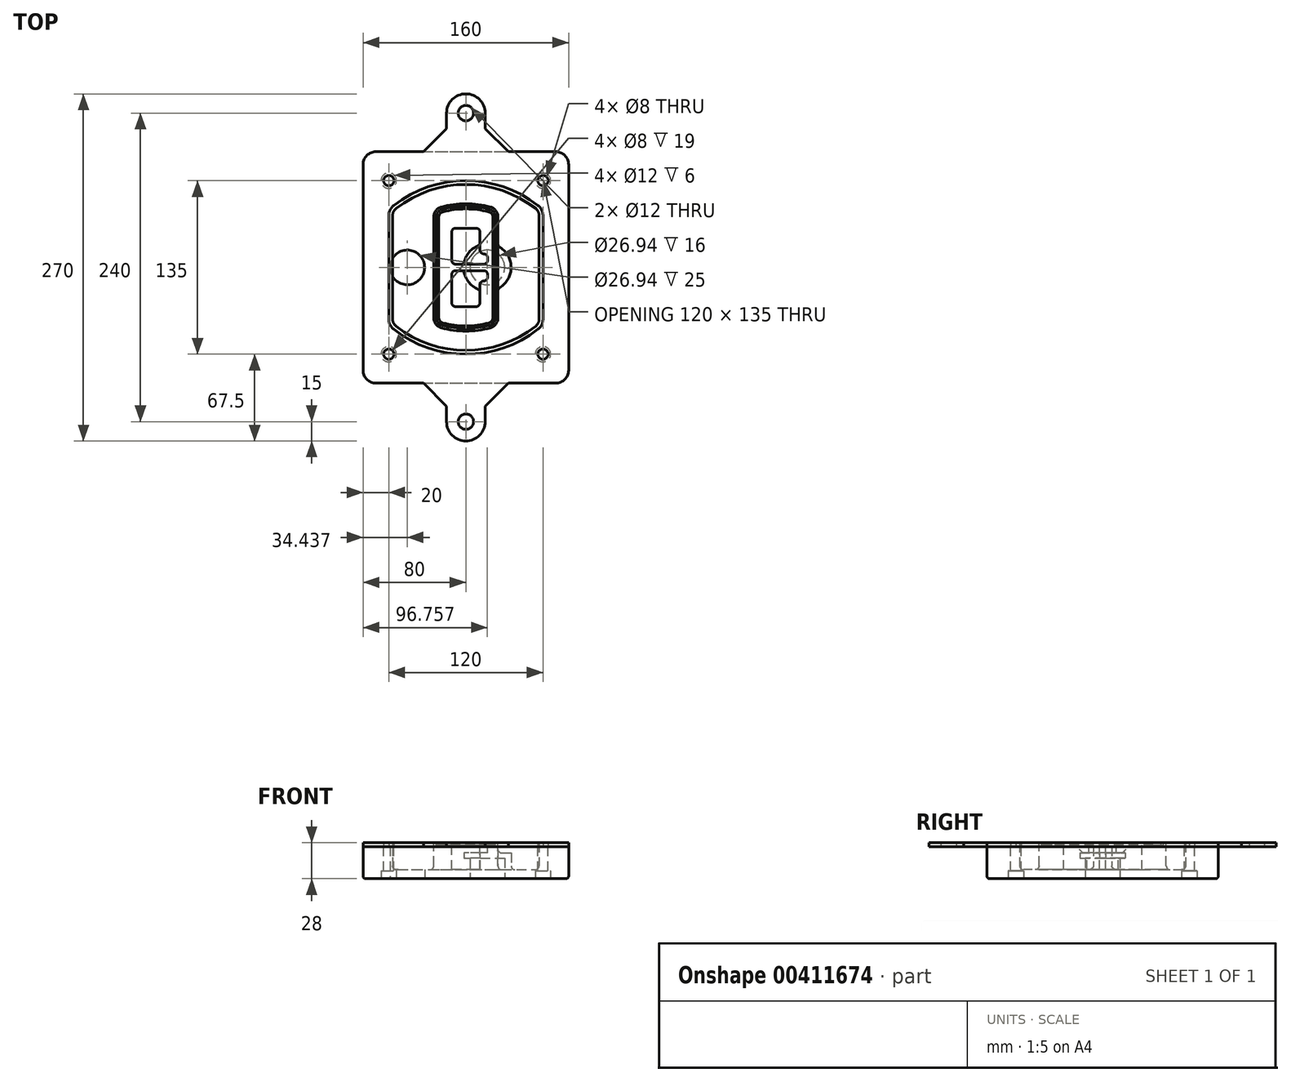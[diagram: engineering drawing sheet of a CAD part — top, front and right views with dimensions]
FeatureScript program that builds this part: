
annotation { "Feature Type Name" : "Feature", "Feature Type Description" : "" }
export const myFeature = defineFeature(function(context is Context, id is Id, definition is map)
    precondition{}
    {
        {
            var Q0;
            Q0=qCreatedBy(makeId("Top.planeOp"),FACE);
            var sketch = newSketch(context, id + "F0", { "sketchPlane" : qUnion([Q0])});
            skPoint(sketch, "E0.rect.middle", {"position": v(0, 0) * mm});
            skLineSegment(sketch, "E1.bottom", {"start": v(-70, -90) * mm, "end": v(70, -90) * mm});
            skLineSegment(sketch, "E1.top", {"start": v(-70, 90) * mm, "end": v(70, 90) * mm});
            skLineSegment(sketch, "E1.left", {"start": v(-80, -80) * mm, "end": v(-80, 80) * mm});
            skLineSegment(sketch, "E1.right", {"start": v(80, -80) * mm, "end": v(80, 80) * mm});
            skLineSegment(sketch, "E2", {"start": v(-80, 90) * mm, "end": v(80, -90) * mm, "construction": true});
            skLineSegment(sketch, "E3", {"start": v(80, 90) * mm, "end": v(-80, -90) * mm, "construction": true});
            skCircle(sketch, "E4", {"center": v(-60, 67.5) * mm, "radius": 4 * mm});
            skCircle(sketch, "E5", {"center": v(60, 67.5) * mm, "radius": 4 * mm});
            skCircle(sketch, "E6", {"center": v(60, -67.5) * mm, "radius": 4 * mm});
            skCircle(sketch, "E7", {"center": v(-60, -67.5) * mm, "radius": 4 * mm});
            skLineSegment(sketch, "E8", {"start": v(-60, 67.5) * mm, "end": v(60, 67.5) * mm, "construction": true});
            skLineSegment(sketch, "E9", {"start": v(60, 67.5) * mm, "end": v(60, -67.5) * mm, "construction": true});
            skLineSegment(sketch, "E10", {"start": v(60, -67.5) * mm, "end": v(-60, -67.5) * mm, "construction": true});
            skLineSegment(sketch, "E11", {"start": v(-60, -67.5) * mm, "end": v(-60, 67.5) * mm, "construction": true});
            skLineSegment(sketch, "E12", {"start": v(-60, 40.3) * mm, "end": v(-60, -40.3) * mm});
            skLineSegment(sketch, "E13", {"start": v(60, 40.3) * mm, "end": v(60, -40.3) * mm});
            skArc(sketch, "E14", {"start": v(56.15, 48.18) * mm, "mid": v(0, 67.5) * mm, "end": v(-56.15, 48.18) * mm});
            skArc(sketch, "E15", {"start": v(-56.15, -48.18) * mm, "mid": v(0, -67.5) * mm, "end": v(56.15, -48.18) * mm});
            skLineSegment(sketch, "E16", {"start": v(-60, 0) * mm, "end": v(60, 0) * mm, "construction": true});
            skPoint(sketch, "E17.visualSharp", {"position": v(-60, -45) * mm});
            skArc(sketch, "E17.filletArc", {"start": v(-60, -40.3) * mm, "mid": v(-58.99, -44.68) * mm, "end": v(-56.15, -48.18) * mm});
            skPoint(sketch, "E18.visualSharp", {"position": v(-60, 45) * mm});
            skArc(sketch, "E18.filletArc", {"start": v(-56.15, 48.18) * mm, "mid": v(-58.99, 44.68) * mm, "end": v(-60, 40.3) * mm});
            skPoint(sketch, "E19.visualSharp", {"position": v(60, 45) * mm});
            skArc(sketch, "E19.filletArc", {"start": v(60, 40.3) * mm, "mid": v(58.99, 44.68) * mm, "end": v(56.15, 48.18) * mm});
            skPoint(sketch, "E20.visualSharp", {"position": v(60, -45) * mm});
            skArc(sketch, "E20.filletArc", {"start": v(56.15, -48.18) * mm, "mid": v(58.99, -44.68) * mm, "end": v(60, -40.3) * mm});
            skPoint(sketch, "E21.visualSharp", {"position": v(-80, 90) * mm});
            skArc(sketch, "E21.filletArc", {"start": v(-70, 90) * mm, "mid": v(-77.07, 87.07) * mm, "end": v(-80, 80) * mm});
            skPoint(sketch, "E22.visualSharp", {"position": v(80, 90) * mm});
            skArc(sketch, "E22.filletArc", {"start": v(80, 80) * mm, "mid": v(77.07, 87.07) * mm, "end": v(70, 90) * mm});
            skPoint(sketch, "E23.visualSharp", {"position": v(80, -90) * mm});
            skArc(sketch, "E23.filletArc", {"start": v(70, -90) * mm, "mid": v(77.07, -87.07) * mm, "end": v(80, -80) * mm});
            skPoint(sketch, "E24.visualSharp", {"position": v(-80, -90) * mm});
            skArc(sketch, "E24.filletArc", {"start": v(-80, -80) * mm, "mid": v(-77.07, -87.07) * mm, "end": v(-70, -90) * mm});
            skArc(sketch, "E25.0", {"start": v(57, 40.3) * mm, "mid": v(56.3, 43.36) * mm, "end": v(54.3, 45.81) * mm});
            skLineSegment(sketch, "E25.1", {"start": v(57, 40.3) * mm, "end": v(57, -40.3) * mm});
            skArc(sketch, "E25.2", {"start": v(54.3, -45.81) * mm, "mid": v(56.3, -43.36) * mm, "end": v(57, -40.3) * mm});
            skArc(sketch, "E25.3", {"start": v(-54.3, -45.81) * mm, "mid": v(0, -64.5) * mm, "end": v(54.3, -45.81) * mm});
            skArc(sketch, "E25.4", {"start": v(-57, -40.3) * mm, "mid": v(-56.3, -43.36) * mm, "end": v(-54.3, -45.81) * mm});
            skArc(sketch, "E25.5", {"start": v(54.3, 45.81) * mm, "mid": v(0, 64.5) * mm, "end": v(-54.3, 45.81) * mm});
            skLineSegment(sketch, "E25.6", {"start": v(-57, 40.3) * mm, "end": v(-57, -40.3) * mm});
            skArc(sketch, "E25.7", {"start": v(-54.3, 45.81) * mm, "mid": v(-56.3, 43.36) * mm, "end": v(-57, 40.3) * mm});
            skArc(sketch, "E26.0", {"start": v(-58.62, 51.33) * mm, "mid": v(-62.58, 46.43) * mm, "end": v(-64, 40.3) * mm});
            skArc(sketch, "E26.1", {"start": v(58.62, 51.33) * mm, "mid": v(0, 71.5) * mm, "end": v(-58.62, 51.33) * mm});
            skArc(sketch, "E26.2", {"start": v(64, 40.3) * mm, "mid": v(62.58, 46.43) * mm, "end": v(58.62, 51.33) * mm});
            skLineSegment(sketch, "E26.3", {"start": v(64, 40.3) * mm, "end": v(64, -40.3) * mm});
            skArc(sketch, "E26.4", {"start": v(58.62, -51.33) * mm, "mid": v(62.58, -46.43) * mm, "end": v(64, -40.3) * mm});
            skLineSegment(sketch, "E26.5", {"start": v(-64, 40.3) * mm, "end": v(-64, -40.3) * mm});
            skArc(sketch, "E26.6", {"start": v(-58.62, -51.33) * mm, "mid": v(0, -71.5) * mm, "end": v(58.62, -51.33) * mm});
            skArc(sketch, "E26.7", {"start": v(-64, -40.3) * mm, "mid": v(-62.58, -46.43) * mm, "end": v(-58.62, -51.33) * mm});
            skSolve(sketch);
        }
        {
            var Q0;
            Q0=makeQuery(id+"F0.imprint","IMPRINT",FACE,{"disambiguationData":[TD([[makeQuery(id+"F0.imprint","IMPRINT",EDGE,{"derivedFrom":sQuery(id+"F0.wireOp",EDGE,"E1.bottom")}),1.0]])]});
            var Q1;
            Q1=makeQuery(id+"F0.imprint","IMPRINT",FACE,{"disambiguationData":[TD([[makeQuery(id+"F0.imprint","IMPRINT",EDGE,{"derivedFrom":sQuery(id+"F0.wireOp",EDGE,"E12")}),1.0]])]});
            var Q2;
            Q2=makeQuery(id+"F0.imprint","IMPRINT",FACE,{"disambiguationData":[TD([[makeQuery(id+"F0.imprint","IMPRINT",EDGE,{"derivedFrom":sQuery(id+"F0.wireOp",EDGE,"E25.0")}),1.0]])]});
            var Q3;
            Q3=makeQuery(id+"F0.imprint","IMPRINT",FACE,{"disambiguationData":[TD([[makeQuery(id+"F0.imprint","IMPRINT",EDGE,{"derivedFrom":sQuery(id+"F0.wireOp",EDGE,"E12")}),-1.0]])]});
            extrude(context, id + "F1", {"entities" : qUnion([Q0, Q1, Q2, Q3]), "oppositeDirection" : true, "depth" : 25 * mm});
        }
        {
            var Q0;
            Q0=makeQuery(id+"F0.imprint","IMPRINT",FACE,{"disambiguationData":[TD([[makeQuery(id+"F0.imprint","IMPRINT",EDGE,{"derivedFrom":sQuery(id+"F0.wireOp",EDGE,"E12")}),1.0]])]});
            extrude(context, id + "F2", {"entities" : qUnion([Q0]), "operationType" : NewBodyOperationType.ADD, "depth" : 3 * mm});
        }
        {
            var Q0;
            Q0=makeQuery(id+"F0.imprint","IMPRINT",FACE,{"disambiguationData":[TD([[makeQuery(id+"F0.imprint","IMPRINT",EDGE,{"derivedFrom":sQuery(id+"F0.wireOp",EDGE,"E25.0")}),1.0]])]});
            extrude(context, id + "F3", {"entities" : qUnion([Q0]), "operationType" : NewBodyOperationType.REMOVE, "oppositeDirection" : true, "depth" : 18 * mm});
        }
        {
            var Q0;
            Q0=makeQuery(id+"F2.opExtrude","CAP_FACE",FACE,{"disambiguationData":[OSD([sQuery(id+"F0.wireOp",EDGE,"E12"),sQuery(id+"F0.wireOp",EDGE,"E13"),sQuery(id+"F0.wireOp",EDGE,"E14"),sQuery(id+"F0.wireOp",EDGE,"E15"),sQuery(id+"F0.wireOp",EDGE,"E17.filletArc"),sQuery(id+"F0.wireOp",EDGE,"E18.filletArc"),sQuery(id+"F0.wireOp",EDGE,"E19.filletArc"),sQuery(id+"F0.wireOp",EDGE,"E20.filletArc"),sQuery(id+"F0.wireOp",EDGE,"E25.0"),sQuery(id+"F0.wireOp",EDGE,"E25.1"),sQuery(id+"F0.wireOp",EDGE,"E25.2"),sQuery(id+"F0.wireOp",EDGE,"E25.3"),sQuery(id+"F0.wireOp",EDGE,"E25.4"),sQuery(id+"F0.wireOp",EDGE,"E25.5"),sQuery(id+"F0.wireOp",EDGE,"E25.6"),sQuery(id+"F0.wireOp",EDGE,"E25.7")])],"isStart":false});
            var sketch = newSketch(context, id + "F4", { "sketchPlane" : qUnion([Q0])});
            skArc(sketch, "E27.0", {"start": v(-19.08, -46.97) * mm, "mid": v(0, -49.5) * mm, "end": v(19.08, -46.97) * mm});
            skArc(sketch, "E28.0", {"start": v(19.08, 46.97) * mm, "mid": v(0, 49.5) * mm, "end": v(-19.08, 46.97) * mm});
            skLineSegment(sketch, "E29", {"start": v(-25, 39.25) * mm, "end": v(-25, -39.25) * mm});
            skLineSegment(sketch, "E30", {"start": v(25, 39.25) * mm, "end": v(25, -39.25) * mm});
            skLineSegment(sketch, "E31", {"start": v(-25, 45.1) * mm, "end": v(25, 45.1) * mm, "construction": true});
            skLineSegment(sketch, "E32", {"start": v(-25, -45.1) * mm, "end": v(25, -45.1) * mm, "construction": true});
            skPoint(sketch, "E33.visualSharp", {"position": v(-25, 45.1) * mm});
            skArc(sketch, "E33.filletArc", {"start": v(-19.08, 46.97) * mm, "mid": v(-23.35, 44.11) * mm, "end": v(-25, 39.25) * mm});
            skPoint(sketch, "E34.visualSharp", {"position": v(25, 45.1) * mm});
            skArc(sketch, "E34.filletArc", {"start": v(25, 39.25) * mm, "mid": v(23.35, 44.11) * mm, "end": v(19.08, 46.97) * mm});
            skPoint(sketch, "E35.visualSharp", {"position": v(25, -45.1) * mm});
            skArc(sketch, "E35.filletArc", {"start": v(19.08, -46.97) * mm, "mid": v(23.35, -44.11) * mm, "end": v(25, -39.25) * mm});
            skPoint(sketch, "E36.visualSharp", {"position": v(-25, -45.1) * mm});
            skArc(sketch, "E36.filletArc", {"start": v(-25, -39.25) * mm, "mid": v(-23.35, -44.11) * mm, "end": v(-19.08, -46.97) * mm});
            skArc(sketch, "E37.0", {"start": v(54.3, 45.81) * mm, "mid": v(0, 64.5) * mm, "end": v(-54.3, 45.81) * mm});
            skArc(sketch, "E37.1", {"start": v(-54.3, 45.81) * mm, "mid": v(-56.3, 43.36) * mm, "end": v(-57, 40.3) * mm});
            skLineSegment(sketch, "E37.2", {"start": v(-57, 40.3) * mm, "end": v(-57, -40.3) * mm});
            skArc(sketch, "E37.3", {"start": v(-57, -40.3) * mm, "mid": v(-56.3, -43.36) * mm, "end": v(-54.3, -45.81) * mm});
            skArc(sketch, "E37.4", {"start": v(-54.3, -45.81) * mm, "mid": v(0, -64.5) * mm, "end": v(54.3, -45.81) * mm});
            skArc(sketch, "E37.5", {"start": v(54.3, -45.81) * mm, "mid": v(56.3, -43.36) * mm, "end": v(57, -40.3) * mm});
            skLineSegment(sketch, "E37.6", {"start": v(57, 40.3) * mm, "end": v(57, -40.3) * mm});
            skArc(sketch, "E37.7", {"start": v(57, 40.3) * mm, "mid": v(56.3, 43.36) * mm, "end": v(54.3, 45.81) * mm});
            skLineSegment(sketch, "E38.0", {"start": v(23, 39.25) * mm, "end": v(23, -39.25) * mm});
            skArc(sketch, "E38.1", {"start": v(18.56, -45.04) * mm, "mid": v(21.76, -42.9) * mm, "end": v(23, -39.25) * mm});
            skArc(sketch, "E38.2", {"start": v(-18.56, -45.04) * mm, "mid": v(0, -47.5) * mm, "end": v(18.56, -45.04) * mm});
            skArc(sketch, "E38.3", {"start": v(-23, -39.25) * mm, "mid": v(-21.76, -42.9) * mm, "end": v(-18.56, -45.04) * mm});
            skLineSegment(sketch, "E38.4", {"start": v(-23, 39.25) * mm, "end": v(-23, -39.25) * mm});
            skArc(sketch, "E38.5", {"start": v(23, 39.25) * mm, "mid": v(21.76, 42.9) * mm, "end": v(18.56, 45.04) * mm});
            skArc(sketch, "E38.6", {"start": v(-18.56, 45.04) * mm, "mid": v(-21.76, 42.9) * mm, "end": v(-23, 39.25) * mm});
            skArc(sketch, "E38.7", {"start": v(18.56, 45.04) * mm, "mid": v(0, 47.5) * mm, "end": v(-18.56, 45.04) * mm});
            skArc(sketch, "E39.0", {"start": v(21, 39.25) * mm, "mid": v(20.18, 41.68) * mm, "end": v(18.04, 43.1) * mm});
            skLineSegment(sketch, "E39.1", {"start": v(21, 39.25) * mm, "end": v(21, -39.25) * mm});
            skArc(sketch, "E39.2", {"start": v(18.04, -43.1) * mm, "mid": v(20.18, -41.68) * mm, "end": v(21, -39.25) * mm});
            skArc(sketch, "E39.3", {"start": v(-18.04, -43.1) * mm, "mid": v(0, -45.5) * mm, "end": v(18.04, -43.1) * mm});
            skArc(sketch, "E39.4", {"start": v(-21, -39.25) * mm, "mid": v(-20.18, -41.68) * mm, "end": v(-18.04, -43.1) * mm});
            skArc(sketch, "E39.5", {"start": v(18.04, 43.1) * mm, "mid": v(0, 45.5) * mm, "end": v(-18.04, 43.1) * mm});
            skLineSegment(sketch, "E39.6", {"start": v(-21, 39.25) * mm, "end": v(-21, -39.25) * mm});
            skArc(sketch, "E39.7", {"start": v(-18.04, 43.1) * mm, "mid": v(-20.18, 41.68) * mm, "end": v(-21, 39.25) * mm});
            skLineSegment(sketch, "E40", {"start": v(-25, 0) * mm, "end": v(25, 0) * mm, "construction": true});
            skLineSegment(sketch, "E41", {"start": v(-11, 5.5) * mm, "end": v(-11, 27.5) * mm});
            skLineSegment(sketch, "E42", {"start": v(-8, 30.5) * mm, "end": v(8, 30.5) * mm});
            skLineSegment(sketch, "E43", {"start": v(11, 27.5) * mm, "end": v(11, 13.5) * mm});
            skLineSegment(sketch, "E44", {"start": v(14, 10.5) * mm, "end": v(14, 10.5) * mm});
            skLineSegment(sketch, "E45", {"start": v(17, 7.5) * mm, "end": v(17, 5.5) * mm});
            skLineSegment(sketch, "E46", {"start": v(14, 2.5) * mm, "end": v(-8, 2.5) * mm});
            skPoint(sketch, "E47.visualSharp", {"position": v(-11, 30.5) * mm});
            skArc(sketch, "E47.filletArc", {"start": v(-8, 30.5) * mm, "mid": v(-10.12, 29.62) * mm, "end": v(-11, 27.5) * mm});
            skPoint(sketch, "E48.visualSharp", {"position": v(11, 30.5) * mm});
            skArc(sketch, "E48.filletArc", {"start": v(11, 27.5) * mm, "mid": v(10.12, 29.62) * mm, "end": v(8, 30.5) * mm});
            skPoint(sketch, "E49.visualSharp", {"position": v(11, 10.5) * mm});
            skArc(sketch, "E49.filletArc", {"start": v(11, 13.5) * mm, "mid": v(11.88, 11.38) * mm, "end": v(14, 10.5) * mm});
            skPoint(sketch, "E50.visualSharp", {"position": v(17, 10.5) * mm});
            skArc(sketch, "E50.filletArc", {"start": v(17, 7.5) * mm, "mid": v(16.12, 9.62) * mm, "end": v(14, 10.5) * mm});
            skPoint(sketch, "E51.visualSharp", {"position": v(17, 2.5) * mm});
            skArc(sketch, "E51.filletArc", {"start": v(14, 2.5) * mm, "mid": v(16.12, 3.38) * mm, "end": v(17, 5.5) * mm});
            skPoint(sketch, "E52.visualSharp", {"position": v(-11, 2.5) * mm});
            skArc(sketch, "E52.filletArc", {"start": v(-11, 5.5) * mm, "mid": v(-10.12, 3.38) * mm, "end": v(-8, 2.5) * mm});
            skLineSegment(sketch, "E53.0.MirrorCS", {"start": v(14, -2.5) * mm, "end": v(-8, -2.5) * mm});
            skArc(sketch, "E54.0.MirrorCS", {"start": v(-11, -5.5) * mm, "mid": v(-10.12, -3.38) * mm, "end": v(-8, -2.5) * mm});
            skLineSegment(sketch, "E55.0.MirrorCS", {"start": v(-11, -5.5) * mm, "end": v(-11, -27.5) * mm});
            skArc(sketch, "E56.0.MirrorCS", {"start": v(-8, -30.5) * mm, "mid": v(-10.12, -29.62) * mm, "end": v(-11, -27.5) * mm});
            skLineSegment(sketch, "E57.0.MirrorCS", {"start": v(-8, -30.5) * mm, "end": v(8, -30.5) * mm});
            skArc(sketch, "E58.0.MirrorCS", {"start": v(11, -27.5) * mm, "mid": v(10.12, -29.62) * mm, "end": v(8, -30.5) * mm});
            skLineSegment(sketch, "E59.0.MirrorCS", {"start": v(11, -27.5) * mm, "end": v(11, -13.5) * mm});
            skArc(sketch, "E60.0.MirrorCS", {"start": v(11, -13.5) * mm, "mid": v(11.88, -11.38) * mm, "end": v(14, -10.5) * mm});
            skArc(sketch, "E61.0.MirrorCS", {"start": v(17, -7.5) * mm, "mid": v(16.12, -9.62) * mm, "end": v(14, -10.5) * mm});
            skLineSegment(sketch, "E62.0.MirrorCS", {"start": v(17, -7.5) * mm, "end": v(17, -5.5) * mm});
            skArc(sketch, "E63.0.MirrorCS", {"start": v(14, -2.5) * mm, "mid": v(16.12, -3.38) * mm, "end": v(17, -5.5) * mm});
            skSolve(sketch);
        }
        {
            var Q0;
            Q0=makeQuery(id+"F4.imprint","IMPRINT",FACE,{"disambiguationData":[TD([[makeQuery(id+"F4.imprint","IMPRINT",EDGE,{"derivedFrom":sQuery(id+"F4.wireOp",EDGE,"E27.0")}),1.0]])]});
            var Q1;
            Q1=makeQuery(id+"F4.imprint","IMPRINT",FACE,{"disambiguationData":[TD([[makeQuery(id+"F4.imprint","IMPRINT",EDGE,{"derivedFrom":sQuery(id+"F4.wireOp",EDGE,"E38.0")}),-1.0]])]});
            var Q2;
            Q2=makeQuery(id+"F4.imprint","IMPRINT",FACE,{"disambiguationData":[TD([[makeQuery(id+"F4.imprint","IMPRINT",EDGE,{"derivedFrom":sQuery(id+"F4.wireOp",EDGE,"E39.0")}),1.0]])]});
            extrude(context, id + "F5", {"entities" : qUnion([Q0, Q1, Q2]), "operationType" : NewBodyOperationType.ADD, "endBound" : BoundingType.UP_TO_NEXT, "oppositeDirection" : true, "depth" : 25 * mm});
        }
        {
            var Q0;
            Q0=makeQuery(id+"F4.imprint","IMPRINT",FACE,{"disambiguationData":[TD([[makeQuery(id+"F4.imprint","IMPRINT",EDGE,{"derivedFrom":sQuery(id+"F4.wireOp",EDGE,"E38.0")}),-1.0]])]});
            extrude(context, id + "F6", {"entities" : qUnion([Q0]), "operationType" : NewBodyOperationType.REMOVE, "oppositeDirection" : true, "depth" : 2 * mm});
        }
        {
            var Q0;
            Q0=makeQuery(id+"F1.opExtrude","CAP_FACE",FACE,{"disambiguationData":[OSD([sQuery(id+"F0.wireOp",EDGE,"E1.bottom"),sQuery(id+"F0.wireOp",EDGE,"E1.top"),sQuery(id+"F0.wireOp",EDGE,"E1.left"),sQuery(id+"F0.wireOp",EDGE,"E1.right"),sQuery(id+"F0.wireOp",EDGE,"E4"),sQuery(id+"F0.wireOp",EDGE,"E5"),sQuery(id+"F0.wireOp",EDGE,"E6"),sQuery(id+"F0.wireOp",EDGE,"E7"),sQuery(id+"F0.wireOp",EDGE,"E21.filletArc"),sQuery(id+"F0.wireOp",EDGE,"E22.filletArc"),sQuery(id+"F0.wireOp",EDGE,"E23.filletArc"),sQuery(id+"F0.wireOp",EDGE,"E24.filletArc")])],"isStart":false});
            var sketch = newSketch(context, id + "F7", { "sketchPlane" : qUnion([Q0])});
            skCircle(sketch, "E64", {"center": v(16.76, 0) * mm, "radius": 13.47 * mm});
            skCircle(sketch, "E65", {"center": v(-45.56, 0) * mm, "radius": 13.47 * mm});
            skLineSegment(sketch, "E66", {"start": v(80, 0) * mm, "end": v(-80, 0) * mm});
            skCircle(sketch, "E67", {"center": v(16.76, 0) * mm, "radius": 18.47 * mm});
            skCircle(sketch, "E68", {"center": v(60, -67.5) * mm, "radius": 6 * mm});
            skCircle(sketch, "E69", {"center": v(-60, -67.5) * mm, "radius": 6 * mm});
            skCircle(sketch, "E70", {"center": v(-60, 67.5) * mm, "radius": 6 * mm});
            skCircle(sketch, "E71", {"center": v(60, 67.5) * mm, "radius": 6 * mm});
            skSolve(sketch);
        }
        {
            var Q0;
            {var subQ1=sQuery(id+"F7.wireOp",EDGE,"E66");var subQ4=sQuery(id+"F7.wireOp",EDGE,"E64");var subQ6=makeQuery(id+"F7.imprint","INTERSECT",VERTEX,{"disambiguationData":[OD(0.0)],"derivedFrom":[subQ4,subQ1]});Q0=makeQuery(id+"F7.imprint","IMPRINT",FACE,{"disambiguationData":[TD([[makeQuery(id+"F7.imprint","IMPRINT",EDGE,{"disambiguationData":[TD([[subQ6,-1.0]])],"derivedFrom":subQ4}),-1.0]])]});}
            var Q1;
            {var subQ0=sQuery(id+"F7.wireOp",EDGE,"E66");var subQ1=sQuery(id+"F7.wireOp",EDGE,"E64");var subQ3=makeQuery(id+"F7.imprint","INTERSECT",VERTEX,{"disambiguationData":[OD(0.0)],"derivedFrom":[subQ1,subQ0]});Q1=makeQuery(id+"F7.imprint","IMPRINT",FACE,{"disambiguationData":[TD([[makeQuery(id+"F7.imprint","IMPRINT",EDGE,{"disambiguationData":[TD([[subQ3,-1.0]])],"derivedFrom":subQ1}),1.0]])]});}
            var Q2;
            {var subQ0=sQuery(id+"F7.wireOp",EDGE,"E66");var subQ1=sQuery(id+"F7.wireOp",EDGE,"E64");var subQ3=makeQuery(id+"F7.imprint","INTERSECT",VERTEX,{"disambiguationData":[OD(0.0)],"derivedFrom":[subQ1,subQ0]});Q2=makeQuery(id+"F7.imprint","IMPRINT",FACE,{"disambiguationData":[TD([[makeQuery(id+"F7.imprint","IMPRINT",EDGE,{"disambiguationData":[TD([[subQ3,1.0]])],"derivedFrom":subQ1}),1.0]])]});}
            var Q3;
            {var subQ1=sQuery(id+"F7.wireOp",EDGE,"E66");var subQ4=sQuery(id+"F7.wireOp",EDGE,"E64");var subQ6=makeQuery(id+"F7.imprint","INTERSECT",VERTEX,{"disambiguationData":[OD(0.0)],"derivedFrom":[subQ4,subQ1]});Q3=makeQuery(id+"F7.imprint","IMPRINT",FACE,{"disambiguationData":[TD([[makeQuery(id+"F7.imprint","IMPRINT",EDGE,{"disambiguationData":[TD([[subQ6,1.0]])],"derivedFrom":subQ4}),-1.0]])]});}
            extrude(context, id + "F8", {"entities" : qUnion([Q0, Q1, Q2, Q3]), "operationType" : NewBodyOperationType.ADD, "oppositeDirection" : true, "depth" : 20 * mm});
        }
        {
            var Q0;
            {var subQ0=sQuery(id+"F7.wireOp",EDGE,"E66");var subQ1=sQuery(id+"F7.wireOp",EDGE,"E64");var subQ3=makeQuery(id+"F7.imprint","INTERSECT",VERTEX,{"disambiguationData":[OD(0.0)],"derivedFrom":[subQ1,subQ0]});Q0=makeQuery(id+"F7.imprint","IMPRINT",FACE,{"disambiguationData":[TD([[makeQuery(id+"F7.imprint","IMPRINT",EDGE,{"disambiguationData":[TD([[subQ3,-1.0]])],"derivedFrom":subQ1}),1.0]])]});}
            var Q1;
            {var subQ0=sQuery(id+"F7.wireOp",EDGE,"E66");var subQ1=sQuery(id+"F7.wireOp",EDGE,"E64");var subQ3=makeQuery(id+"F7.imprint","INTERSECT",VERTEX,{"disambiguationData":[OD(0.0)],"derivedFrom":[subQ1,subQ0]});Q1=makeQuery(id+"F7.imprint","IMPRINT",FACE,{"disambiguationData":[TD([[makeQuery(id+"F7.imprint","IMPRINT",EDGE,{"disambiguationData":[TD([[subQ3,1.0]])],"derivedFrom":subQ1}),1.0]])]});}
            extrude(context, id + "F9", {"entities" : qUnion([Q0, Q1]), "operationType" : NewBodyOperationType.REMOVE, "oppositeDirection" : true, "depth" : 16 * mm});
        }
        {
            var Q0;
            {var subQ0=sQuery(id+"F7.wireOp",EDGE,"E66");var subQ1=sQuery(id+"F7.wireOp",EDGE,"E65");var subQ3=makeQuery(id+"F7.imprint","INTERSECT",VERTEX,{"disambiguationData":[OD(0.0)],"derivedFrom":[subQ1,subQ0]});Q0=makeQuery(id+"F7.imprint","IMPRINT",FACE,{"disambiguationData":[TD([[makeQuery(id+"F7.imprint","IMPRINT",EDGE,{"disambiguationData":[TD([[subQ3,-1.0]])],"derivedFrom":subQ1}),1.0]])]});}
            var Q1;
            {var subQ0=sQuery(id+"F7.wireOp",EDGE,"E66");var subQ1=sQuery(id+"F7.wireOp",EDGE,"E65");var subQ3=makeQuery(id+"F7.imprint","INTERSECT",VERTEX,{"disambiguationData":[OD(0.0)],"derivedFrom":[subQ1,subQ0]});Q1=makeQuery(id+"F7.imprint","IMPRINT",FACE,{"disambiguationData":[TD([[makeQuery(id+"F7.imprint","IMPRINT",EDGE,{"disambiguationData":[TD([[subQ3,1.0]])],"derivedFrom":subQ1}),1.0]])]});}
            extrude(context, id + "F10", {"entities" : qUnion([Q0, Q1]), "operationType" : NewBodyOperationType.REMOVE, "oppositeDirection" : true, "depth" : 25 * mm});
        }
        {
            var Q0;
            Q0=makeQuery(id+"F7.imprint","IMPRINT",FACE,{"disambiguationData":[TD([[makeQuery(id+"F7.imprint","IMPRINT",EDGE,{"derivedFrom":sQuery(id+"F7.wireOp",EDGE,"E68")}),1.0]])]});
            var Q1;
            Q1=makeQuery(id+"F7.imprint","IMPRINT",FACE,{"disambiguationData":[TD([[makeQuery(id+"F7.imprint","IMPRINT",EDGE,{"derivedFrom":makeQuery(id+"F1.opExtrude","CAP_EDGE",EDGE,{"disambiguationData":[OSD([sQuery(id+"F0.wireOp",EDGE,"E5")])],"isStart":false})}),-1.0]])]});
            var Q2;
            Q2=makeQuery(id+"F7.imprint","IMPRINT",FACE,{"disambiguationData":[TD([[makeQuery(id+"F7.imprint","IMPRINT",EDGE,{"derivedFrom":sQuery(id+"F7.wireOp",EDGE,"E69")}),1.0]])]});
            var Q3;
            Q3=makeQuery(id+"F7.imprint","IMPRINT",FACE,{"disambiguationData":[TD([[makeQuery(id+"F7.imprint","IMPRINT",EDGE,{"derivedFrom":makeQuery(id+"F1.opExtrude","CAP_EDGE",EDGE,{"disambiguationData":[OSD([sQuery(id+"F0.wireOp",EDGE,"E4")])],"isStart":false})}),-1.0]])]});
            var Q4;
            Q4=makeQuery(id+"F7.imprint","IMPRINT",FACE,{"disambiguationData":[TD([[makeQuery(id+"F7.imprint","IMPRINT",EDGE,{"derivedFrom":sQuery(id+"F7.wireOp",EDGE,"E70")}),1.0]])]});
            var Q5;
            Q5=makeQuery(id+"F7.imprint","IMPRINT",FACE,{"disambiguationData":[TD([[makeQuery(id+"F7.imprint","IMPRINT",EDGE,{"derivedFrom":makeQuery(id+"F1.opExtrude","CAP_EDGE",EDGE,{"disambiguationData":[OSD([sQuery(id+"F0.wireOp",EDGE,"E7")])],"isStart":false})}),-1.0]])]});
            var Q6;
            Q6=makeQuery(id+"F7.imprint","IMPRINT",FACE,{"disambiguationData":[TD([[makeQuery(id+"F7.imprint","IMPRINT",EDGE,{"derivedFrom":sQuery(id+"F7.wireOp",EDGE,"E71")}),1.0]])]});
            var Q7;
            Q7=makeQuery(id+"F7.imprint","IMPRINT",FACE,{"disambiguationData":[TD([[makeQuery(id+"F7.imprint","IMPRINT",EDGE,{"derivedFrom":makeQuery(id+"F1.opExtrude","CAP_EDGE",EDGE,{"disambiguationData":[OSD([sQuery(id+"F0.wireOp",EDGE,"E6")])],"isStart":false})}),-1.0]])]});
            extrude(context, id + "F11", {"entities" : qUnion([Q0, Q1, Q2, Q3, Q4, Q5, Q6, Q7]), "operationType" : NewBodyOperationType.REMOVE, "oppositeDirection" : true, "depth" : 6 * mm});
        }
        {
            var Q0;
            Q0=makeQuery(id+"F9.boolean.opBoolean","COPY",FACE,{"derivedFrom":makeQuery(id+"F9.opExtrude","CAP_FACE",FACE,{"disambiguationData":[OSD([sQuery(id+"F7.wireOp",EDGE,"E64")])],"isStart":false})});
            var sketch = newSketch(context, id + "F12", { "sketchPlane" : qUnion([Q0])});
            skArc(sketch, "E72.0", {"start": v(11, 17.55) * mm, "mid": v(2.57, 11.82) * mm, "end": v(-1.54, 2.5) * mm});
            skArc(sketch, "E72.1", {"start": v(-1.54, -2.5) * mm, "mid": v(2.57, -11.82) * mm, "end": v(11, -17.55) * mm});
            skLineSegment(sketch, "E73", {"start": v(-1.54, -2.5) * mm, "end": v(14, -2.5) * mm});
            skLineSegment(sketch, "E74.0", {"start": v(14, 2.5) * mm, "end": v(-1.54, 2.5) * mm});
            skArc(sketch, "E74.1", {"start": v(14, 2.5) * mm, "mid": v(16.12, 3.38) * mm, "end": v(17, 5.5) * mm});
            skLineSegment(sketch, "E74.2", {"start": v(17, 7.5) * mm, "end": v(17, 5.5) * mm});
            skArc(sketch, "E74.3", {"start": v(17, 7.5) * mm, "mid": v(16.12, 9.62) * mm, "end": v(14, 10.5) * mm});
            skArc(sketch, "E74.4", {"start": v(11, 13.5) * mm, "mid": v(11.88, 11.38) * mm, "end": v(14, 10.5) * mm});
            skLineSegment(sketch, "E74.5", {"start": v(11, 17.55) * mm, "end": v(11, 13.5) * mm});
            skLineSegment(sketch, "E74.7", {"start": v(14, -2.5) * mm, "end": v(-1.54, -2.5) * mm});
            skArc(sketch, "E74.8", {"start": v(14, -2.5) * mm, "mid": v(16.12, -3.38) * mm, "end": v(17, -5.5) * mm});
            skLineSegment(sketch, "E74.9", {"start": v(17, -7.5) * mm, "end": v(17, -5.5) * mm});
            skArc(sketch, "E74.10", {"start": v(17, -7.5) * mm, "mid": v(16.12, -9.62) * mm, "end": v(14, -10.5) * mm});
            skArc(sketch, "E74.11", {"start": v(11, -13.5) * mm, "mid": v(11.88, -11.38) * mm, "end": v(14, -10.5) * mm});
            skLineSegment(sketch, "E74.12", {"start": v(11, -17.55) * mm, "end": v(11, -13.5) * mm});
            skPoint(sketch, "E75.orphan", {"position": v(11, -27.5) * mm});
            skPoint(sketch, "E76.orphan", {"position": v(-8, -2.5) * mm});
            skPoint(sketch, "E77.orphan", {"position": v(-8, 2.5) * mm});
            skPoint(sketch, "E78.orphan", {"position": v(11, 27.5) * mm});
            skSolve(sketch);
        }
        {
            var Q0;
            {var subQ7=sQuery(id+"F12.wireOp",EDGE,"E72.0");var subQ14=sQuery(id+"F12.wireOp",EDGE,"E72.1");var subQ16=sQuery(id+"F12.wireOp",EDGE,"E74.1");var subQ18=sQuery(id+"F12.wireOp",EDGE,"E74.8");Q0=qUnion([makeQuery(id+"F12.imprint","IMPRINT",FACE,{"disambiguationData":[TD([[makeQuery(id+"F12.imprint","IMPRINT",EDGE,{"derivedFrom":subQ7}),1.0]])]}),makeQuery(id+"F12.imprint","IMPRINT",FACE,{"disambiguationData":[TD([[makeQuery(id+"F12.imprint","IMPRINT",EDGE,{"derivedFrom":subQ14}),1.0]])]}),makeQuery(id+"F12.imprint","IMPRINT",FACE,{"disambiguationData":[TD([[makeQuery(id+"F12.imprint","IMPRINT",EDGE,{"derivedFrom":subQ16}),1.0]])]}),makeQuery(id+"F12.imprint","IMPRINT",FACE,{"disambiguationData":[TD([[makeQuery(id+"F12.imprint","IMPRINT",EDGE,{"derivedFrom":subQ18}),-1.0]])]})]);}
            var Q1;
            Q1=makeQuery(id+"F5.boolean.opBoolean","SPLIT",FACE,{"disambiguationData":[TD([makeQuery(id+"F5.opExtrude","SWEPT_FACE",FACE,{"disambiguationData":[OSD([sQuery(id+"F4.wireOp",EDGE,"E41")])]})])],"derivedFrom":makeQuery(id+"F3.boolean.opBoolean","COPY",FACE,{"derivedFrom":makeQuery(id+"F3.opExtrude","CAP_FACE",FACE,{"disambiguationData":[OSD([sQuery(id+"F0.wireOp",EDGE,"E25.0"),sQuery(id+"F0.wireOp",EDGE,"E25.1"),sQuery(id+"F0.wireOp",EDGE,"E25.2"),sQuery(id+"F0.wireOp",EDGE,"E25.3"),sQuery(id+"F0.wireOp",EDGE,"E25.4"),sQuery(id+"F0.wireOp",EDGE,"E25.5"),sQuery(id+"F0.wireOp",EDGE,"E25.6"),sQuery(id+"F0.wireOp",EDGE,"E25.7")])],"isStart":false})})});
            extrude(context, id + "F13", {"entities" : qUnion([Q0]), "operationType" : NewBodyOperationType.REMOVE, "endBound" : BoundingType.UP_TO_SURFACE, "endBoundEntityFace" : qUnion([Q1]), "depth" : 25 * mm});
        }
        {
            var Q0;
            Q0=makeQuery(id+"F3.boolean.opBoolean","COPY",EDGE,{"derivedFrom":makeQuery(id+"F3.opExtrude","CAP_EDGE",EDGE,{"disambiguationData":[OSD([sQuery(id+"F0.wireOp",EDGE,"E25.6")])],"isStart":false})});
            var Q1;
            Q1=makeQuery(id+"F8.boolean.opBoolean","INTERSECT",EDGE,{"derivedFrom":[makeQuery(id+"F5.opExtrude","SWEPT_FACE",FACE,{"disambiguationData":[OSD([sQuery(id+"F4.wireOp",EDGE,"E30")])]}),makeQuery(id+"F8.opExtrude","CAP_FACE",FACE,{"disambiguationData":[OSD([sQuery(id+"F7.wireOp",EDGE,"E67")])],"isStart":false})]});
            var Q2;
            Q2=makeQuery(id+"F8.boolean.opBoolean","INTERSECT",EDGE,{"disambiguationData":[OD(1.0)],"derivedFrom":[makeQuery(id+"F5.opExtrude","SWEPT_FACE",FACE,{"disambiguationData":[OSD([sQuery(id+"F4.wireOp",EDGE,"E30")])]}),makeQuery(id+"F8.opExtrude","SWEPT_FACE",FACE,{"disambiguationData":[OSD([sQuery(id+"F7.wireOp",EDGE,"E67")])]})]});
            var Q3;
            {var subQ0=sQuery(id+"F4.wireOp",EDGE,"E30");Q3=makeQuery(id+"F8.boolean.opBoolean","SPLIT",EDGE,{"disambiguationData":[TD([makeQuery(id+"F5.opExtrude","SWEPT_FACE",FACE,{"disambiguationData":[OSD([sQuery(id+"F4.wireOp",EDGE,"E35.filletArc")])]})])],"derivedFrom":makeQuery(id+"F5.opExtrude","CAP_EDGE",EDGE,{"disambiguationData":[OSD([subQ0])],"isStart":false})});}
            var Q4;
            {var subQ0=sQuery(id+"F0.wireOp",EDGE,"E25.7");var subQ1=sQuery(id+"F0.wireOp",EDGE,"E25.1");var subQ2=sQuery(id+"F0.wireOp",EDGE,"E25.6");var subQ3=sQuery(id+"F0.wireOp",EDGE,"E25.5");var subQ4=sQuery(id+"F0.wireOp",EDGE,"E25.4");var subQ5=sQuery(id+"F0.wireOp",EDGE,"E25.0");var subQ6=sQuery(id+"F0.wireOp",EDGE,"E25.2");var subQ7=sQuery(id+"F0.wireOp",EDGE,"E25.3");Q4=makeQuery(id+"F8.boolean.opBoolean","INTERSECT",EDGE,{"derivedFrom":[makeQuery(id+"F5.boolean.opBoolean","SPLIT",FACE,{"disambiguationData":[TD([makeQuery(id+"F2.opExtrude","SWEPT_FACE",FACE,{"disambiguationData":[OSD([subQ5])]})])],"derivedFrom":makeQuery(id+"F3.boolean.opBoolean","COPY",FACE,{"derivedFrom":makeQuery(id+"F3.opExtrude","CAP_FACE",FACE,{"disambiguationData":[OSD([subQ5,subQ1,subQ6,subQ7,subQ4,subQ3,subQ2,subQ0])],"isStart":false})})}),makeQuery(id+"F8.opExtrude","SWEPT_FACE",FACE,{"disambiguationData":[OSD([sQuery(id+"F7.wireOp",EDGE,"E67")])]})]});}
            var Q5;
            Q5=makeQuery(id+"F8.boolean.opBoolean","INTERSECT",EDGE,{"disambiguationData":[OD(0.0)],"derivedFrom":[makeQuery(id+"F5.opExtrude","SWEPT_FACE",FACE,{"disambiguationData":[OSD([sQuery(id+"F4.wireOp",EDGE,"E30")])]}),makeQuery(id+"F8.opExtrude","SWEPT_FACE",FACE,{"disambiguationData":[OSD([sQuery(id+"F7.wireOp",EDGE,"E67")])]})]});
            fillet(context, id + "F14", {"entities" : qUnion([Q0, Q1, Q2, Q3, Q4, Q5]), "radius" : 3 * mm, "tangentPropagation" : true, "allowEdgeOverflow" : false});
        }
        {
            var Q0;
            Q0=makeQuery(id+"F1.opExtrude","CAP_EDGE",EDGE,{"disambiguationData":[OSD([sQuery(id+"F0.wireOp",EDGE,"E1.bottom")])],"isStart":false});
            fillet(context, id + "F15", {"entities" : qUnion([Q0]), "radius" : 2 * mm, "tangentPropagation" : true, "allowEdgeOverflow" : false});
        }
        {
            var Q0;
            Q0=qCreatedBy(makeId("Top.planeOp"),FACE);
            var sketch = newSketch(context, id + "F16", { "sketchPlane" : qUnion([Q0])});
            skLineSegment(sketch, "E79.0", {"start": v(-70, 90) * mm, "end": v(70, 90) * mm});
            skArc(sketch, "E79.1", {"start": v(-70, 90) * mm, "mid": v(-77.07, 87.07) * mm, "end": v(-80, 80) * mm});
            skLineSegment(sketch, "E79.2", {"start": v(-80, -80) * mm, "end": v(-80, 80) * mm});
            skArc(sketch, "E79.3", {"start": v(-80, -80) * mm, "mid": v(-77.07, -87.07) * mm, "end": v(-70, -90) * mm});
            skLineSegment(sketch, "E79.4", {"start": v(-70, -90) * mm, "end": v(70, -90) * mm});
            skArc(sketch, "E79.5", {"start": v(70, -90) * mm, "mid": v(77.07, -87.07) * mm, "end": v(80, -80) * mm});
            skLineSegment(sketch, "E79.6", {"start": v(80, -80) * mm, "end": v(80, 80) * mm});
            skArc(sketch, "E79.7", {"start": v(80, 80) * mm, "mid": v(77.07, 87.07) * mm, "end": v(70, 90) * mm});
            skCircle(sketch, "E79.8", {"center": v(-60, 67.5) * mm, "radius": 4 * mm});
            skCircle(sketch, "E79.9", {"center": v(60, 67.5) * mm, "radius": 4 * mm});
            skCircle(sketch, "E79.10", {"center": v(60, -67.5) * mm, "radius": 4 * mm});
            skCircle(sketch, "E79.11", {"center": v(-60, -67.5) * mm, "radius": 4 * mm});
            skArc(sketch, "E79.12", {"start": v(-56.15, -48.18) * mm, "mid": v(0, -67.5) * mm, "end": v(56.15, -48.18) * mm});
            skArc(sketch, "E79.13", {"start": v(-60, -40.3) * mm, "mid": v(-58.99, -44.68) * mm, "end": v(-56.15, -48.18) * mm});
            skLineSegment(sketch, "E79.14", {"start": v(-60, 40.3) * mm, "end": v(-60, -40.3) * mm});
            skArc(sketch, "E79.15", {"start": v(-56.15, 48.18) * mm, "mid": v(-58.99, 44.68) * mm, "end": v(-60, 40.3) * mm});
            skArc(sketch, "E79.16", {"start": v(56.15, 48.18) * mm, "mid": v(0, 67.5) * mm, "end": v(-56.15, 48.18) * mm});
            skArc(sketch, "E79.17", {"start": v(60, 40.3) * mm, "mid": v(58.99, 44.68) * mm, "end": v(56.15, 48.18) * mm});
            skLineSegment(sketch, "E79.18", {"start": v(60, 40.3) * mm, "end": v(60, -40.3) * mm});
            skArc(sketch, "E79.19", {"start": v(56.15, -48.18) * mm, "mid": v(58.99, -44.68) * mm, "end": v(60, -40.3) * mm});
            skLineSegment(sketch, "E80", {"start": v(0, 90) * mm, "end": v(0, 120) * mm, "construction": true});
            skLineSegment(sketch, "E81", {"start": v(-33, 90) * mm, "end": v(-15, 108) * mm});
            skLineSegment(sketch, "E82", {"start": v(-15, 108) * mm, "end": v(-15, 120) * mm});
            skArc(sketch, "E83", {"start": v(15, 120) * mm, "mid": v(0, 135) * mm, "end": v(-15, 120) * mm});
            skLineSegment(sketch, "E84", {"start": v(15, 120) * mm, "end": v(15, 108) * mm});
            skLineSegment(sketch, "E85", {"start": v(15, 108) * mm, "end": v(33, 90) * mm});
            skCircle(sketch, "E86", {"center": v(0, 120) * mm, "radius": 6 * mm});
            skLineSegment(sketch, "E87", {"start": v(-80, 0) * mm, "end": v(80, 0) * mm, "construction": true});
            skLineSegment(sketch, "E88.MirrorCS", {"start": v(-15, -108) * mm, "end": v(-15, -120) * mm});
            skLineSegment(sketch, "E89.MirrorCS", {"start": v(15, -120) * mm, "end": v(15, -108) * mm});
            skCircle(sketch, "E90.MirrorC", {"center": v(0, -120) * mm, "radius": 6 * mm});
            skArc(sketch, "E91.MirrorCS", {"start": v(15, -120) * mm, "mid": v(0, -135) * mm, "end": v(-15, -120) * mm});
            skLineSegment(sketch, "E92.MirrorCS", {"start": v(-33, -90) * mm, "end": v(-15, -108) * mm});
            skLineSegment(sketch, "E93.MirrorCS", {"start": v(15, -108) * mm, "end": v(33, -90) * mm});
            skLineSegment(sketch, "E94.MirrorCS", {"start": v(0, -90) * mm, "end": v(0, -120) * mm, "construction": true});
            skSolve(sketch);
        }
        {
            var Q0;
            Q0 = qSketchRegion(id + "F16", true);
            var Q1;
            Q1=makeQuery(id+"F2.opExtrude","CAP_FACE",FACE,{"disambiguationData":[OSD([sQuery(id+"F0.wireOp",EDGE,"E12"),sQuery(id+"F0.wireOp",EDGE,"E13"),sQuery(id+"F0.wireOp",EDGE,"E14"),sQuery(id+"F0.wireOp",EDGE,"E15"),sQuery(id+"F0.wireOp",EDGE,"E17.filletArc"),sQuery(id+"F0.wireOp",EDGE,"E18.filletArc"),sQuery(id+"F0.wireOp",EDGE,"E19.filletArc"),sQuery(id+"F0.wireOp",EDGE,"E20.filletArc"),sQuery(id+"F0.wireOp",EDGE,"E25.0"),sQuery(id+"F0.wireOp",EDGE,"E25.1"),sQuery(id+"F0.wireOp",EDGE,"E25.2"),sQuery(id+"F0.wireOp",EDGE,"E25.3"),sQuery(id+"F0.wireOp",EDGE,"E25.4"),sQuery(id+"F0.wireOp",EDGE,"E25.5"),sQuery(id+"F0.wireOp",EDGE,"E25.6"),sQuery(id+"F0.wireOp",EDGE,"E25.7")])],"isStart":false});
            extrude(context, id + "F17", {"entities" : qUnion([Q0]), "endBound" : BoundingType.UP_TO_SURFACE, "endBoundEntityFace" : qUnion([Q1]), "depth" : 25 * mm});
        }
    });
